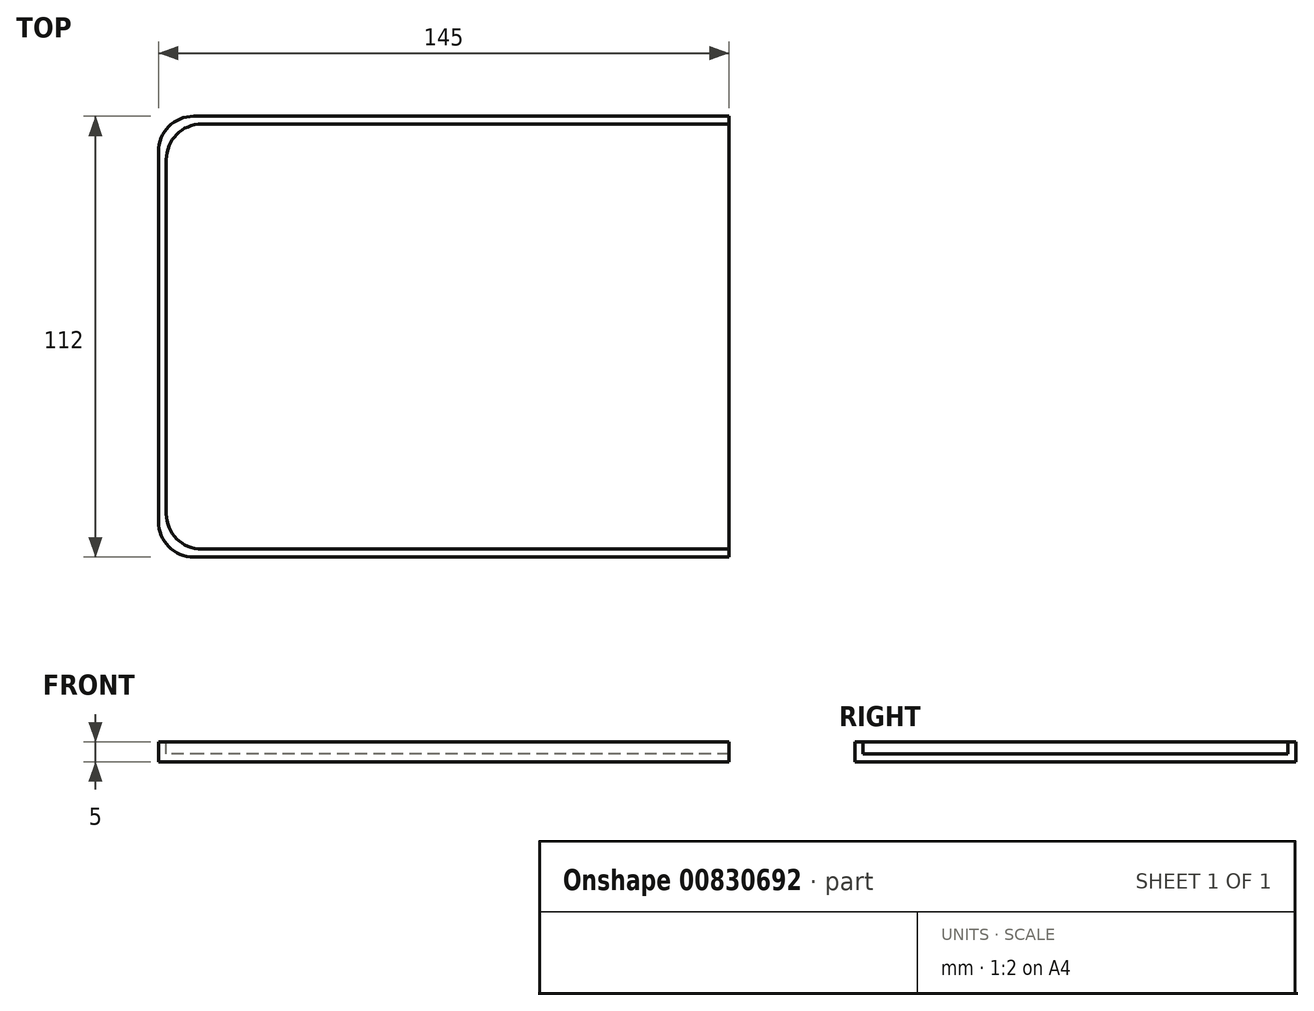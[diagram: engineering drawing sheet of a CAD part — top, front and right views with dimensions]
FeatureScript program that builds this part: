
annotation { "Feature Type Name" : "Feature", "Feature Type Description" : "" }
export const myFeature = defineFeature(function(context is Context, id is Id, definition is map)
    precondition{}
    {
        {
            var Q0;
            Q0=qCreatedBy(makeId("Top.planeOp"),FACE);
            var sketch = newSketch(context, id + "F0", { "sketchPlane" : qUnion([Q0])});
            skLineSegment(sketch, "E0.bottom", {"start": v(-86, -56) * mm, "end": v(50, -56) * mm});
            skLineSegment(sketch, "E0.top", {"start": v(-86, 56) * mm, "end": v(50, 56) * mm});
            skLineSegment(sketch, "E0.left", {"start": v(-95, -47) * mm, "end": v(-95, 47) * mm});
            skPoint(sketch, "E1.visualSharp", {"position": v(95, 56) * mm});
            skPoint(sketch, "E2.visualSharp", {"position": v(95, -56) * mm});
            skPoint(sketch, "E3.visualSharp", {"position": v(-95, -56) * mm});
            skArc(sketch, "E3.filletArc", {"start": v(-95, -47) * mm, "mid": v(-92.36, -53.36) * mm, "end": v(-86, -56) * mm});
            skPoint(sketch, "E4.visualSharp", {"position": v(-95, 56) * mm});
            skArc(sketch, "E4.filletArc", {"start": v(-86, 56) * mm, "mid": v(-92.36, 53.36) * mm, "end": v(-95, 47) * mm});
            skLineSegment(sketch, "E5", {"start": v(50, -56) * mm, "end": v(50, 56) * mm});
            skPoint(sketch, "E1.filletArc.end.orphan", {"position": v(186, 56) * mm});
            skPoint(sketch, "E6.orphan", {"position": v(186, -56) * mm});
            skSolve(sketch);
        }
        {
            var Q0;
            Q0=qSketchRegion(id+"F0",true);
            extrude(context, id + "F1", {"entities" : qUnion([Q0]), "depth" : 5 * mm, "offsetDistance" : 25 * mm});
        }
        {
            var Q0;
            Q0=makeQuery(id+"F1.opExtrude","CAP_FACE",FACE,{"disambiguationData":[OSD([sQuery(id+"F0.wireOp",EDGE,"E0.bottom"),sQuery(id+"F0.wireOp",EDGE,"E0.top"),sQuery(id+"F0.wireOp",EDGE,"E0.left"),sQuery(id+"F0.wireOp",EDGE,"E3.filletArc"),sQuery(id+"F0.wireOp",EDGE,"E4.filletArc"),sQuery(id+"F0.wireOp",EDGE,"E5")])],"isStart":false});
            var sketch = newSketch(context, id + "F2", { "sketchPlane" : qUnion([Q0])});
            skLineSegment(sketch, "E7", {"start": v(50, 54) * mm, "end": v(-84, 54) * mm});
            skLineSegment(sketch, "E8", {"start": v(50, -54) * mm, "end": v(-84, -54) * mm});
            skLineSegment(sketch, "E9", {"start": v(-93, 45) * mm, "end": v(-93, -45) * mm});
            skLineSegment(sketch, "E10", {"start": v(50, -54) * mm, "end": v(50, 54) * mm});
            skArc(sketch, "E11.filletArc", {"start": v(-84, 54) * mm, "mid": v(-90.36, 51.36) * mm, "end": v(-93, 45) * mm});
            skArc(sketch, "E12.filletArc", {"start": v(-93, -45) * mm, "mid": v(-90.36, -51.36) * mm, "end": v(-84, -54) * mm});
            skSolve(sketch);
        }
        {
            var Q0;
            Q0=makeQuery(id+"F2.imprint","IMPRINT",FACE,{"disambiguationData":[TD([[makeQuery(id+"F2.imprint","IMPRINT",EDGE,{"derivedFrom":sQuery(id+"F2.wireOp",EDGE,"E7")}),1.0]])]});
            extrude(context, id + "F3", {"entities" : qUnion([Q0]), "operationType" : NewBodyOperationType.REMOVE, "oppositeDirection" : true, "depth" : 3 * mm, "offsetDistance" : 25 * mm});
        }
    });
